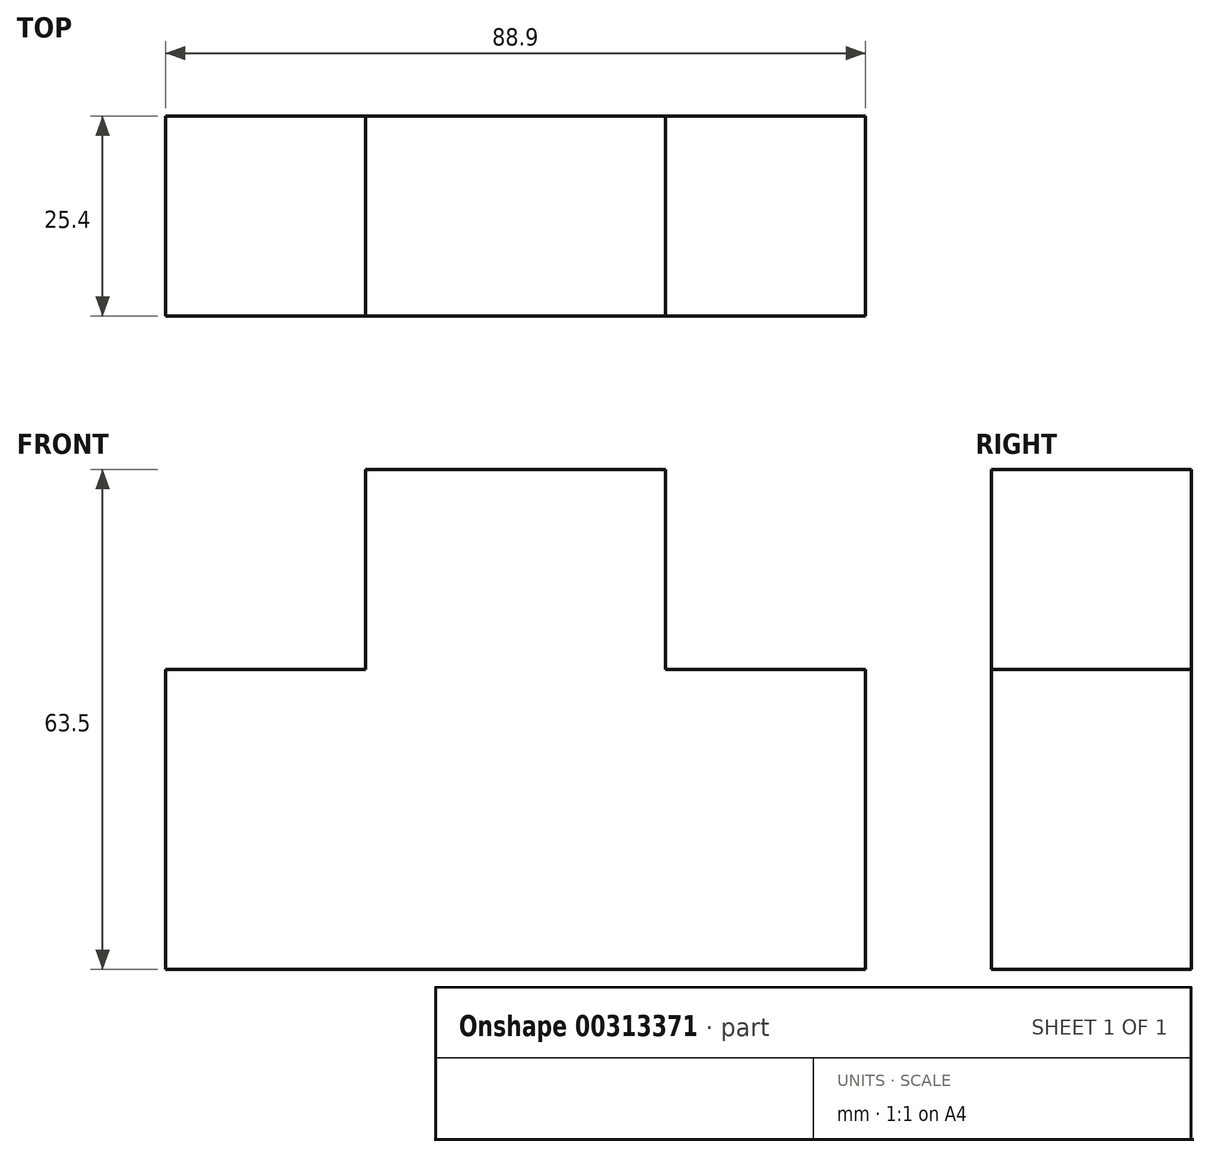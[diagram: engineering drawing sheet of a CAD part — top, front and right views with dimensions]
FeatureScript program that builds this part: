
annotation { "Feature Type Name" : "Feature", "Feature Type Description" : "" }
export const myFeature = defineFeature(function(context is Context, id is Id, definition is map)
    precondition{}
    {
        {
            var Q0;
            Q0=qCreatedBy(makeId("Front.planeOp"),FACE);
            var sketch = newSketch(context, id + "F0", { "sketchPlane" : qUnion([Q0])});
            skLineSegment(sketch, "E0", {"start": v(-42.02, -28.5) * mm, "end": v(46.88, -28.5) * mm});
            skLineSegment(sketch, "E1", {"start": v(-42.02, -28.5) * mm, "end": v(-42.02, 9.6) * mm});
            skLineSegment(sketch, "E2", {"start": v(-42.02, 9.6) * mm, "end": v(-16.62, 9.6) * mm});
            skLineSegment(sketch, "E3", {"start": v(-16.62, 9.6) * mm, "end": v(-16.62, 35) * mm});
            skLineSegment(sketch, "E4", {"start": v(-16.62, 35) * mm, "end": v(21.48, 35) * mm});
            skLineSegment(sketch, "E5", {"start": v(21.48, 35) * mm, "end": v(21.48, 9.6) * mm});
            skLineSegment(sketch, "E6", {"start": v(21.48, 9.6) * mm, "end": v(46.88, 9.6) * mm});
            skLineSegment(sketch, "E7", {"start": v(46.88, 9.6) * mm, "end": v(46.88, -28.5) * mm});
            skSolve(sketch);
        }
        {
            var Q0;
            Q0=makeQuery(id+"F0.imprint","IMPRINT",FACE,{"disambiguationData":[TD([[makeQuery(id+"F0.imprint","IMPRINT",EDGE,{"derivedFrom":sQuery(id+"F0.wireOp",EDGE,"E0")}),1.0]])]});
            extrude(context, id + "F1", {"entities" : qUnion([Q0]), "depth" : 25.4 * mm});
        }
    });
